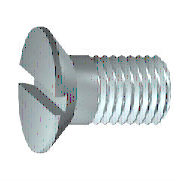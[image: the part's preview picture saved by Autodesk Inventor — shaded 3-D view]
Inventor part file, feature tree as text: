
AUTODESK INVENTOR PART (.ipt)
format: ipt  version: 2017 SP1 (Build 210196100, 196)  size: 188,416 bytes
history: native  units: mm (DEFAULTED — no unit token found)
features: sketch x2, extrude x1, fillet x1, plane x1
ambient origin geometry x7: Origin, YZ Plane, XZ Plane, X Axis, Y Axis, Z Axis, Center Point
bodies: Solid1 (feature_tree), Body (feature_tree)
feature tree (5):
  extrude  "Slot"  Depth=6.35mm
  fillet  "Radius"  Radius=6.35mm
  plane  "Work Plane1"
  sketch  "Sketch1"  dims[d0=19.05mm d1=7.15585mm d2=1.27mm d3=12.319mm d4=3.556mm d5=6.35mm d6=6.35mm]
  sketch  "Sketch2"  dims[d7=11.4808mm d19=90.0deg d8=1.7272mm d9=0.0mm d10=12.319mm d11=0.0mm d12=0.75565mm d13=0.635mm d15=1.905mm d16=11.4808mm d17=0.0mm d35=45.0deg d39=0.0mm d40=0.0mm d41=2.54mm]
